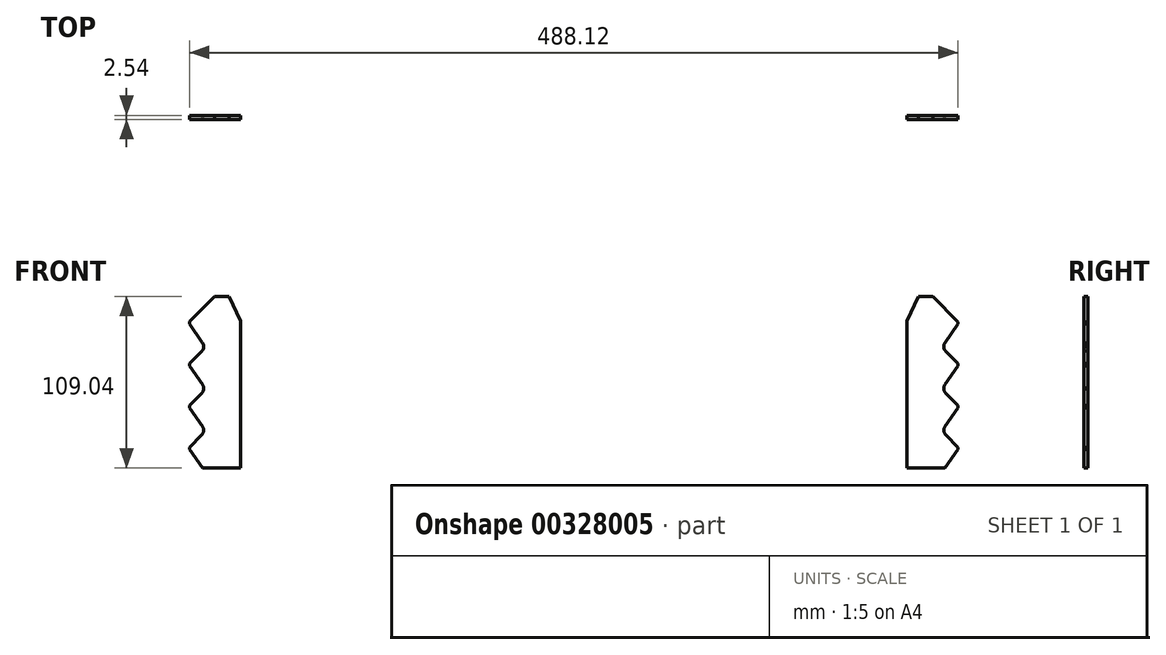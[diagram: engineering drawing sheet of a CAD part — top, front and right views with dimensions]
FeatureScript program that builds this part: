
annotation { "Feature Type Name" : "Feature", "Feature Type Description" : "" }
export const myFeature = defineFeature(function(context is Context, id is Id, definition is map)
    precondition{}
    {
        {
            var Q0;
            Q0=qCreatedBy(makeId("Front.planeOp"),FACE);
            var sketch = newSketch(context, id + "F0", { "sketchPlane" : qUnion([Q0])});
            skPoint(sketch, "E0.MirrorP", {"position": v(235.84, 0) * mm});
            skLineSegment(sketch, "E1.MirrorCS", {"start": v(211.54, 0) * mm, "end": v(211.54, 93.5) * mm});
            skLineSegment(sketch, "E2.MirrorCS", {"start": v(211.54, 0) * mm, "end": v(235.84, 0) * mm});
            skLineSegment(sketch, "E3.MirrorCS", {"start": v(218.8, 109.04) * mm, "end": v(228, 109.04) * mm});
            skLineSegment(sketch, "E4.MirrorCS", {"start": v(244.06, 92.99) * mm, "end": v(244.06, 91.47) * mm});
            skLineSegment(sketch, "E5", {"start": v(235.84, 0) * mm, "end": v(244.06, 11.73) * mm});
            skLineSegment(sketch, "E6", {"start": v(244.06, 13.26) * mm, "end": v(236.31, 21) * mm});
            skLineSegment(sketch, "E7", {"start": v(244.06, 38.28) * mm, "end": v(235.83, 26.53) * mm});
            skLineSegment(sketch, "E8", {"start": v(235.04, 50.92) * mm, "end": v(235.04, 50.32) * mm});
            skLineSegment(sketch, "E9", {"start": v(244.06, 39.8) * mm, "end": v(236.3, 47.56) * mm});
            skLineSegment(sketch, "E10", {"start": v(244.06, 64.87) * mm, "end": v(235.8, 53.1) * mm});
            skLineSegment(sketch, "E11", {"start": v(244.06, 66.4) * mm, "end": v(236.14, 74.3) * mm});
            skLineSegment(sketch, "E12", {"start": v(244.06, 91.47) * mm, "end": v(235.69, 79.52) * mm});
            skLineSegment(sketch, "E13", {"start": v(235.04, 76.85) * mm, "end": v(235.04, 77.58) * mm});
            skLineSegment(sketch, "E14", {"start": v(244.06, 92.99) * mm, "end": v(228, 109.04) * mm});
            skLineSegment(sketch, "E15.trimOffspring", {"start": v(244.06, 13.26) * mm, "end": v(244.06, 11.73) * mm});
            skLineSegment(sketch, "E16.trimOffspring", {"start": v(244.06, 39.8) * mm, "end": v(244.06, 38.28) * mm});
            skLineSegment(sketch, "E17.trimOffspring", {"start": v(244.06, 66.4) * mm, "end": v(244.06, 64.87) * mm});
            skArc(sketch, "E18", {"start": v(235.83, 26.53) * mm, "mid": v(235.07, 23.68) * mm, "end": v(236.31, 21) * mm});
            skLineSegment(sketch, "E19", {"start": v(218.8, 109.04) * mm, "end": v(211.54, 93.5) * mm});
            skLineSegment(sketch, "E20", {"start": v(0, 0) * mm, "end": v(0, 28.33) * mm});
            skLineSegment(sketch, "E21", {"start": v(239.35, 77.21) * mm, "end": v(235.93, 79.86) * mm});
            skArc(sketch, "E22", {"start": v(235.93, 79.86) * mm, "mid": v(235.04, 76.83) * mm, "end": v(236.44, 74) * mm});
            skLineSegment(sketch, "E23", {"start": v(239.35, 50.62) * mm, "end": v(235.8, 53.1) * mm});
            skArc(sketch, "E24", {"start": v(235.8, 53.1) * mm, "mid": v(235.04, 50.24) * mm, "end": v(236.3, 47.56) * mm});
            skLineSegment(sketch, "E25.MirrorCS", {"start": v(-244.06, 93.02) * mm, "end": v(-244.06, 91.47) * mm});
            skLineSegment(sketch, "E26.MirrorCS", {"start": v(-244.06, 92.99) * mm, "end": v(-244.06, 91.47) * mm});
            skLineSegment(sketch, "E27.MirrorCS", {"start": v(-244.06, 92.99) * mm, "end": v(-243.17, 93.87) * mm});
            skLineSegment(sketch, "E28.MirrorCS", {"start": v(-244.06, 13.26) * mm, "end": v(-244.06, 11.73) * mm});
            skLineSegment(sketch, "E29.MirrorCS", {"start": v(-218.8, 109.04) * mm, "end": v(-228.03, 109.04) * mm});
            skLineSegment(sketch, "E30.MirrorCS", {"start": v(-235.84, 0) * mm, "end": v(-244.06, 11.73) * mm});
            skLineSegment(sketch, "E31.MirrorCS", {"start": v(-244.06, 13.26) * mm, "end": v(-236.31, 21) * mm});
            skLineSegment(sketch, "E32.MirrorCS", {"start": v(-244.06, 39.8) * mm, "end": v(-244.06, 38.28) * mm});
            skLineSegment(sketch, "E33.MirrorCS", {"start": v(-211.54, 0) * mm, "end": v(-235.84, 0) * mm});
            skLineSegment(sketch, "E34.MirrorCS", {"start": v(-244.07, 93) * mm, "end": v(-228.03, 109.04) * mm});
            skLineSegment(sketch, "E35.MirrorCS", {"start": v(-218.8, 109.04) * mm, "end": v(-211.54, 93.5) * mm});
            skLineSegment(sketch, "E36.MirrorCS", {"start": v(-244.06, 39.8) * mm, "end": v(-236.3, 47.56) * mm});
            skLineSegment(sketch, "E37.MirrorCS", {"start": v(-239.35, 50.62) * mm, "end": v(-235.8, 53.1) * mm});
            skLineSegment(sketch, "E38.MirrorCS", {"start": v(-235.04, 76.85) * mm, "end": v(-235.04, 77.58) * mm});
            skLineSegment(sketch, "E39.MirrorCS", {"start": v(-244.06, 66.4) * mm, "end": v(-244.06, 64.87) * mm});
            skArc(sketch, "E40.MirrorCS", {"start": v(-235.83, 26.53) * mm, "mid": v(-235.07, 23.68) * mm, "end": v(-236.31, 21) * mm});
            skLineSegment(sketch, "E41.MirrorCS", {"start": v(-235.04, 50.92) * mm, "end": v(-235.04, 50.32) * mm});
            skLineSegment(sketch, "E42.MirrorCS", {"start": v(-244.06, 66.4) * mm, "end": v(-236.14, 74.3) * mm});
            skArc(sketch, "E43.MirrorCS", {"start": v(-235.8, 53.1) * mm, "mid": v(-235.04, 50.24) * mm, "end": v(-236.3, 47.56) * mm});
            skLineSegment(sketch, "E44.MirrorCS", {"start": v(-244.06, 38.28) * mm, "end": v(-235.83, 26.53) * mm});
            skLineSegment(sketch, "E45.MirrorCS", {"start": v(-244.06, 64.87) * mm, "end": v(-235.8, 53.1) * mm});
            skLineSegment(sketch, "E46.MirrorCS", {"start": v(-211.54, 0) * mm, "end": v(-211.54, 93.5) * mm});
            skArc(sketch, "E47.MirrorCS", {"start": v(-235.93, 79.86) * mm, "mid": v(-235.04, 76.83) * mm, "end": v(-236.44, 74) * mm});
            skLineSegment(sketch, "E48.MirrorCS", {"start": v(-244.06, 91.47) * mm, "end": v(-235.69, 79.52) * mm});
            skLineSegment(sketch, "E49.MirrorCS", {"start": v(-239.35, 77.21) * mm, "end": v(-235.93, 79.86) * mm});
            skPoint(sketch, "E50.MirrorP", {"position": v(-235.84, 0) * mm});
            skPoint(sketch, "E51.orphan", {"position": v(243.17, 93.87) * mm});
            skSolve(sketch);
        }
        {
            var Q0;
            Q0=makeQuery(id+"F0.imprint","IMPRINT",FACE,{"disambiguationData":[TD([[makeQuery(id+"F0.imprint","IMPRINT",EDGE,{"derivedFrom":sQuery(id+"F0.wireOp",EDGE,"E2.MirrorCS")}),1.0]])]});
            var Q1;
            Q1=makeQuery(id+"F0.imprint","IMPRINT",FACE,{"disambiguationData":[TD([[makeQuery(id+"F0.imprint","IMPRINT",EDGE,{"derivedFrom":sQuery(id+"F0.wireOp",EDGE,"E30.MirrorCS")}),-1.0]])]});
            var Q2;
            {var subQ0=sQuery(id+"F0.wireOp",EDGE,"E22");var subQ1=sQuery(id+"F0.wireOp",EDGE,"E11");var subQ2=makeQuery(id+"F0.imprint","INTERSECT",VERTEX,{"disambiguationData":[OD(0.0)],"derivedFrom":[subQ1,subQ0]});Q2=makeQuery(id+"F0.imprint","IMPRINT",FACE,{"disambiguationData":[TD([[makeQuery(id+"F0.imprint","IMPRINT",EDGE,{"disambiguationData":[TD([[subQ2,1.0]])],"derivedFrom":subQ1}),1.0]])]});}
            var Q3;
            {var subQ0=sQuery(id+"F0.wireOp",EDGE,"E41.MirrorCS");Q3=makeQuery(id+"F0.imprint","IMPRINT",FACE,{"disambiguationData":[TD([[makeQuery(id+"F0.imprint","IMPRINT",EDGE,{"derivedFrom":subQ0}),1.0]])]});}
            var Q4;
            {var subQ0=sQuery(id+"F0.wireOp",EDGE,"E13");Q4=makeQuery(id+"F0.imprint","IMPRINT",FACE,{"disambiguationData":[TD([[makeQuery(id+"F0.imprint","IMPRINT",EDGE,{"derivedFrom":subQ0}),1.0]])]});}
            var Q5;
            {var subQ0=sQuery(id+"F0.wireOp",EDGE,"E22");var subQ1=sQuery(id+"F0.wireOp",EDGE,"E12");var subQ2=makeQuery(id+"F0.imprint","INTERSECT",VERTEX,{"disambiguationData":[OD(0.0)],"derivedFrom":[subQ1,subQ0]});Q5=makeQuery(id+"F0.imprint","IMPRINT",FACE,{"disambiguationData":[TD([[makeQuery(id+"F0.imprint","IMPRINT",EDGE,{"disambiguationData":[TD([[subQ2,1.0]])],"derivedFrom":subQ1}),-1.0]])]});}
            var Q6;
            {var subQ0=sQuery(id+"F0.wireOp",EDGE,"E8");Q6=makeQuery(id+"F0.imprint","IMPRINT",FACE,{"disambiguationData":[TD([[makeQuery(id+"F0.imprint","IMPRINT",EDGE,{"derivedFrom":subQ0}),-1.0]])]});}
            var Q7;
            {var subQ0=sQuery(id+"F0.wireOp",EDGE,"E47.MirrorCS");var subQ1=sQuery(id+"F0.wireOp",EDGE,"E42.MirrorCS");var subQ2=makeQuery(id+"F0.imprint","INTERSECT",VERTEX,{"disambiguationData":[OD(0.0)],"derivedFrom":[subQ1,subQ0]});Q7=makeQuery(id+"F0.imprint","IMPRINT",FACE,{"disambiguationData":[TD([[makeQuery(id+"F0.imprint","IMPRINT",EDGE,{"disambiguationData":[TD([[subQ2,1.0]])],"derivedFrom":subQ1}),-1.0]])]});}
            var Q8;
            {var subQ0=sQuery(id+"F0.wireOp",EDGE,"E38.MirrorCS");Q8=makeQuery(id+"F0.imprint","IMPRINT",FACE,{"disambiguationData":[TD([[makeQuery(id+"F0.imprint","IMPRINT",EDGE,{"derivedFrom":subQ0}),-1.0]])]});}
            var Q9;
            {var subQ0=sQuery(id+"F0.wireOp",EDGE,"E48.MirrorCS");var subQ1=sQuery(id+"F0.wireOp",EDGE,"E47.MirrorCS");var subQ2=makeQuery(id+"F0.imprint","INTERSECT",VERTEX,{"disambiguationData":[OD(0.0)],"derivedFrom":[subQ1,subQ0]});Q9=makeQuery(id+"F0.imprint","IMPRINT",FACE,{"disambiguationData":[TD([[makeQuery(id+"F0.imprint","IMPRINT",EDGE,{"disambiguationData":[TD([[subQ2,-1.0]])],"derivedFrom":subQ1}),-1.0]])]});}
            extrude(context, id + "F1", {"entities" : qUnion([Q0, Q1, Q2, Q3, Q4, Q5, Q6, Q7, Q8, Q9]), "depth" : 2.54 * mm});
        }
    });
